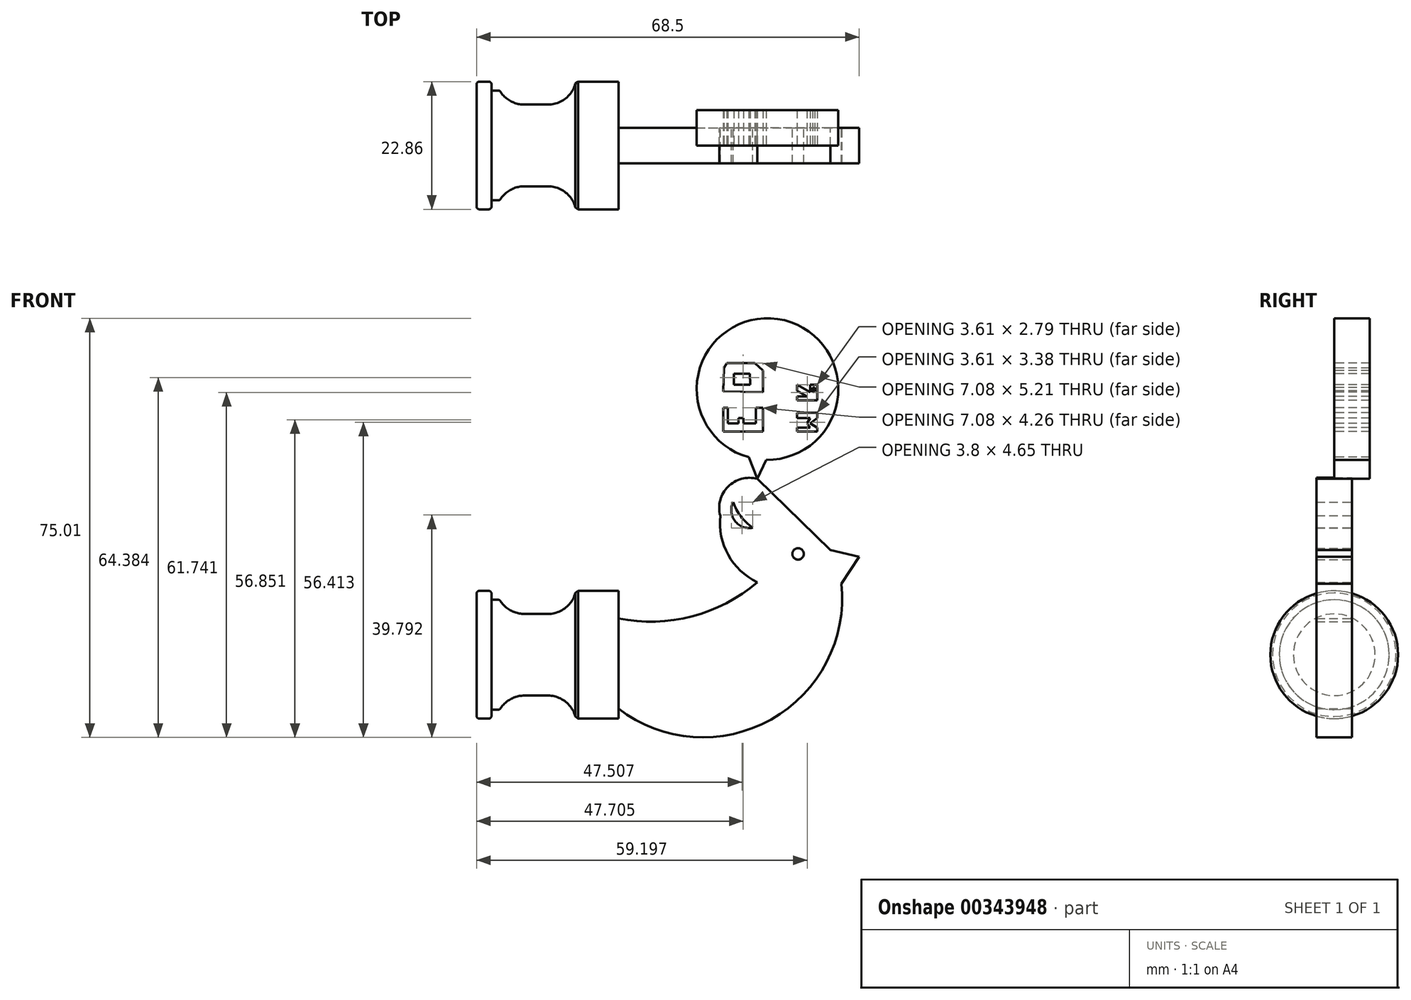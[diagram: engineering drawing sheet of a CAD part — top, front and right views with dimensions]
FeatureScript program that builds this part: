
annotation { "Feature Type Name" : "Feature", "Feature Type Description" : "" }
export const myFeature = defineFeature(function(context is Context, id is Id, definition is map)
    precondition{}
    {
        {
            var Q0;
            Q0=qCreatedBy(makeId("Front.planeOp"),FACE);
            var sketch = newSketch(context, id + "F0", { "sketchPlane" : qUnion([Q0])});
            skLineSegment(sketch, "E0", {"start": v(0, 0) * mm, "end": v(-25.4, 0) * mm});
            skLineSegment(sketch, "E1", {"start": v(-25.4, 0) * mm, "end": v(-25.4, 11.43) * mm});
            skLineSegment(sketch, "E2", {"start": v(-25.4, 11.43) * mm, "end": v(-22.71, 11.43) * mm});
            skLineSegment(sketch, "E3", {"start": v(-22.71, 11.43) * mm, "end": v(-22.71, 9.84) * mm});
            skLineSegment(sketch, "E4", {"start": v(-22.71, 9.84) * mm, "end": v(-21.25, 9.84) * mm});
            skLineSegment(sketch, "E5", {"start": v(-21.25, 9.84) * mm, "end": v(-20.32, 7.31) * mm});
            skLineSegment(sketch, "E6", {"start": v(-20.32, 7.31) * mm, "end": v(-7.62, 7.31) * mm});
            skLineSegment(sketch, "E7", {"start": v(-7.62, 7.31) * mm, "end": v(-7.62, 11.43) * mm});
            skLineSegment(sketch, "E8", {"start": v(-7.62, 11.43) * mm, "end": v(0, 11.43) * mm});
            skLineSegment(sketch, "E9", {"start": v(0, 11.43) * mm, "end": v(0, 0) * mm});
            skSolve(sketch);
        }
        {
            var Q0;
            Q0=makeQuery(id+"F0.imprint","IMPRINT",FACE,{"disambiguationData":[TD([[makeQuery(id+"F0.imprint","IMPRINT",EDGE,{"derivedFrom":sQuery(id+"F0.wireOp",EDGE,"E0")}),-1.0]])]});
            var Q1;
            Q1=sQuery(id+"F0.wireOp",EDGE,"E0");
            revolve(context, id + "F1", {"entities" : qUnion([Q0]), "axis" : qUnion([Q1]), "revolveType" : RevolveType.FULL});
        }
        {
            var Q0;
            Q0=makeQuery(id+"F1.opRevolve","SWEPT_EDGE",EDGE,{"disambiguationData":[OSD([sQuery(id+"F0.wireOp",EDGE,"E5"),sQuery(id+"F0.wireOp",EDGE,"E6")])]});
            fillet(context, id + "F2", {"entities" : qUnion([Q0]), "radius" : 5.08 * mm, "tangentPropagation" : true, "allowEdgeOverflow" : false});
        }
        {
            var Q0;
            Q0=makeQuery(id+"F1.opRevolve","SWEPT_EDGE",EDGE,{"disambiguationData":[OSD([sQuery(id+"F0.wireOp",EDGE,"E6"),sQuery(id+"F0.wireOp",EDGE,"E7")])]});
            fillet(context, id + "F3", {"entities" : qUnion([Q0]), "radius" : 5.08 * mm, "tangentPropagation" : true, "allowEdgeOverflow" : false});
        }
        {
            var Q0;
            Q0=makeQuery(id+"F2.opFillet","BLEND_EDGE",EDGE,{"blendedFrom":[makeQuery(id+"F1.opRevolve","SWEPT_EDGE",EDGE,{"disambiguationData":[OSD([sQuery(id+"F0.wireOp",EDGE,"E5"),sQuery(id+"F0.wireOp",EDGE,"E6")])]}),makeQuery(id+"F1.opRevolve","SWEPT_FACE",FACE,{"disambiguationData":[OSD([sQuery(id+"F0.wireOp",EDGE,"E4")])]})],"blendedInto":[makeQuery(id+"F1.opRevolve","SWEPT_FACE",FACE,{"disambiguationData":[OSD([sQuery(id+"F0.wireOp",EDGE,"E4")])]})]});
            var Q1;
            Q1=makeQuery(id+"F1.opRevolve","SWEPT_EDGE",EDGE,{"disambiguationData":[OSD([sQuery(id+"F0.wireOp",EDGE,"E2"),sQuery(id+"F0.wireOp",EDGE,"E3")])]});
            var Q2;
            Q2=makeQuery(id+"F1.opRevolve","SWEPT_EDGE",EDGE,{"disambiguationData":[OSD([sQuery(id+"F0.wireOp",EDGE,"E1"),sQuery(id+"F0.wireOp",EDGE,"E2")])]});
            fillet(context, id + "F4", {"entities" : qUnion([Q0, Q1, Q2]), "radius" : 0.5 * mm, "tangentPropagation" : true, "allowEdgeOverflow" : false});
        }
        {
            var Q0;
            {var subQ0=sQuery(id+"F0.wireOp",EDGE,"E9");var subQ1=sQuery(id+"F0.wireOp",EDGE,"E8");var subQ2=makeQuery(id+"F1.opRevolve","SWEPT_EDGE",EDGE,{"disambiguationData":[OSD([subQ1,subQ0])]});Q0=makeQuery(id+"F3.opFillet","BLEND_EDGE",EDGE,{"blendedFrom":[makeQuery(id+"F1.opRevolve","SWEPT_EDGE",EDGE,{"disambiguationData":[OSD([sQuery(id+"F0.wireOp",EDGE,"E6"),sQuery(id+"F0.wireOp",EDGE,"E7")])]}),makeQuery(id+"FKdUeLkxdvxAeGn_1.boolean.opBoolean","MERGE",FACE,{"derivedFrom":[makeQuery(id+"F1.opRevolve","SWEPT_FACE",FACE,{"disambiguationData":[OSD([subQ1])]}),makeQuery(id+"FKdUeLkxdvxAeGn_1.opExtrude","SWEPT_FACE",FACE,{"disambiguationData":[OSD([subQ1,subQ0]),TDD([makeQuery(id+"FhPrJ5y7E5olnpu_1.imprint","IMPRINT",EDGE,{"disambiguationData":[TD([[makeQuery(id+"FhPrJ5y7E5olnpu_1.imprint","INTERSECT",VERTEX,{"derivedFrom":[subQ2,sQuery(id+"FhPrJ5y7E5olnpu_1.wireOp",EDGE,"5swccAFu-Qq9y-H5FG-WLZN-0cyFNXjqbd3L")]}),1.0]])],"derivedFrom":subQ2})])]}),makeQuery(id+"FKdUeLkxdvxAeGn_1.opExtrude","SWEPT_FACE",FACE,{"disambiguationData":[OSD([subQ1,subQ0]),TDD([makeQuery(id+"FhPrJ5y7E5olnpu_1.imprint","IMPRINT",EDGE,{"disambiguationData":[TD([[makeQuery(id+"FhPrJ5y7E5olnpu_1.imprint","INTERSECT",VERTEX,{"derivedFrom":[subQ2,sQuery(id+"FhPrJ5y7E5olnpu_1.wireOp",EDGE,"yrlBlJsE-glzK-ckup-w4H4-O8etLDBYbZ2E")]}),1.0]])],"derivedFrom":subQ2})])]}),makeQuery(id+"FKdUeLkxdvxAeGn_1.opExtrude","SWEPT_FACE",FACE,{"disambiguationData":[OSD([subQ1,subQ0]),TDD([makeQuery(id+"FhPrJ5y7E5olnpu_1.imprint","IMPRINT",EDGE,{"disambiguationData":[TD([[makeQuery(id+"FhPrJ5y7E5olnpu_1.imprint","INTERSECT",VERTEX,{"derivedFrom":[subQ2,sQuery(id+"FhPrJ5y7E5olnpu_1.wireOp",EDGE,"59esLNOy-bGTi-q598-Dafd-GjDcgzXxW0rH")]}),-1.0]])],"derivedFrom":subQ2})])]}),makeQuery(id+"FKdUeLkxdvxAeGn_1.opExtrude","SWEPT_FACE",FACE,{"disambiguationData":[OSD([subQ1,subQ0]),TDD([makeQuery(id+"FhPrJ5y7E5olnpu_1.imprint","IMPRINT",EDGE,{"disambiguationData":[TD([[makeQuery(id+"FhPrJ5y7E5olnpu_1.imprint","INTERSECT",VERTEX,{"derivedFrom":[subQ2,sQuery(id+"FhPrJ5y7E5olnpu_1.wireOp",EDGE,"8v8Xe1NO-uW00-CEbA-Of9p-lGgIFj4n3XNv")]}),-1.0]])],"derivedFrom":subQ2})])]})]})],"blendedInto":[makeQuery(id+"FKdUeLkxdvxAeGn_1.boolean.opBoolean","MERGE",FACE,{"derivedFrom":[makeQuery(id+"F1.opRevolve","SWEPT_FACE",FACE,{"disambiguationData":[OSD([subQ1])]}),makeQuery(id+"FKdUeLkxdvxAeGn_1.opExtrude","SWEPT_FACE",FACE,{"disambiguationData":[OSD([subQ1,subQ0]),TDD([makeQuery(id+"FhPrJ5y7E5olnpu_1.imprint","IMPRINT",EDGE,{"disambiguationData":[TD([[makeQuery(id+"FhPrJ5y7E5olnpu_1.imprint","INTERSECT",VERTEX,{"derivedFrom":[subQ2,sQuery(id+"FhPrJ5y7E5olnpu_1.wireOp",EDGE,"5swccAFu-Qq9y-H5FG-WLZN-0cyFNXjqbd3L")]}),1.0]])],"derivedFrom":subQ2})])]}),makeQuery(id+"FKdUeLkxdvxAeGn_1.opExtrude","SWEPT_FACE",FACE,{"disambiguationData":[OSD([subQ1,subQ0]),TDD([makeQuery(id+"FhPrJ5y7E5olnpu_1.imprint","IMPRINT",EDGE,{"disambiguationData":[TD([[makeQuery(id+"FhPrJ5y7E5olnpu_1.imprint","INTERSECT",VERTEX,{"derivedFrom":[subQ2,sQuery(id+"FhPrJ5y7E5olnpu_1.wireOp",EDGE,"yrlBlJsE-glzK-ckup-w4H4-O8etLDBYbZ2E")]}),1.0]])],"derivedFrom":subQ2})])]}),makeQuery(id+"FKdUeLkxdvxAeGn_1.opExtrude","SWEPT_FACE",FACE,{"disambiguationData":[OSD([subQ1,subQ0]),TDD([makeQuery(id+"FhPrJ5y7E5olnpu_1.imprint","IMPRINT",EDGE,{"disambiguationData":[TD([[makeQuery(id+"FhPrJ5y7E5olnpu_1.imprint","INTERSECT",VERTEX,{"derivedFrom":[subQ2,sQuery(id+"FhPrJ5y7E5olnpu_1.wireOp",EDGE,"59esLNOy-bGTi-q598-Dafd-GjDcgzXxW0rH")]}),-1.0]])],"derivedFrom":subQ2})])]}),makeQuery(id+"FKdUeLkxdvxAeGn_1.opExtrude","SWEPT_FACE",FACE,{"disambiguationData":[OSD([subQ1,subQ0]),TDD([makeQuery(id+"FhPrJ5y7E5olnpu_1.imprint","IMPRINT",EDGE,{"disambiguationData":[TD([[makeQuery(id+"FhPrJ5y7E5olnpu_1.imprint","INTERSECT",VERTEX,{"derivedFrom":[subQ2,sQuery(id+"FhPrJ5y7E5olnpu_1.wireOp",EDGE,"8v8Xe1NO-uW00-CEbA-Of9p-lGgIFj4n3XNv")]}),-1.0]])],"derivedFrom":subQ2})])]})]})]});}
            chamfer(context, id + "F5", {"entities" : qUnion([Q0]), "width" : 0.5 * mm, "tangentPropagation" : true});
        }
        {
            var Q0;
            Q0=qCreatedBy(makeId("Front.planeOp"),FACE);
            var sketch = newSketch(context, id + "F6", { "sketchPlane" : qUnion([Q0])});
            skArc(sketch, "E10", {"start": v(0, -9.66) * mm, "mid": v(27.32, -11.6) * mm, "end": v(39.92, 12.73) * mm});
            skLineSegment(sketch, "E11", {"start": v(39.92, 12.73) * mm, "end": v(43.1, 17.57) * mm});
            skLineSegment(sketch, "E12", {"start": v(43.1, 17.57) * mm, "end": v(37.92, 18.75) * mm});
            skLineSegment(sketch, "E13", {"start": v(37.92, 18.75) * mm, "end": v(24.83, 31.48) * mm});
            skArc(sketch, "E14", {"start": v(24.83, 31.48) * mm, "mid": v(19.62, 30.1) * mm, "end": v(18.23, 24.88) * mm});
            skArc(sketch, "E15", {"start": v(18.23, 24.88) * mm, "mid": v(19.65, 17.88) * mm, "end": v(24.83, 12.97) * mm});
            skArc(sketch, "E16", {"start": v(0, 6.5) * mm, "mid": v(13.16, 6.87) * mm, "end": v(24.83, 12.97) * mm});
            skLineSegment(sketch, "E17", {"start": v(0, -9.66) * mm, "end": v(0, 6.5) * mm});
            skSolve(sketch);
        }
        {
            var Q0;
            Q0=makeQuery(id+"F6.imprint","IMPRINT",FACE,{"disambiguationData":[TD([[makeQuery(id+"F6.imprint","IMPRINT",EDGE,{"derivedFrom":sQuery(id+"F6.wireOp",EDGE,"E10")}),1.0]])]});
            extrude(context, id + "F7", {"entities" : qUnion([Q0]), "operationType" : NewBodyOperationType.ADD, "endBound" : BoundingType.SYMMETRIC, "depth" : 6.35 * mm});
        }
        {
            var Q0;
            Q0=makeQuery(id+"F7.opExtrude","CAP_FACE",FACE,{"disambiguationData":[OSD([sQuery(id+"F6.wireOp",EDGE,"E10"),sQuery(id+"F6.wireOp",EDGE,"E11"),sQuery(id+"F6.wireOp",EDGE,"E12"),sQuery(id+"F6.wireOp",EDGE,"E13"),sQuery(id+"F6.wireOp",EDGE,"E14"),sQuery(id+"F6.wireOp",EDGE,"E15"),sQuery(id+"F6.wireOp",EDGE,"E16"),sQuery(id+"F6.wireOp",EDGE,"E17")])],"isStart":true});
            var sketch = newSketch(context, id + "F8", { "sketchPlane" : qUnion([Q0])});
            skCircle(sketch, "E18", {"center": v(-32.15, 18.05) * mm, "radius": 1.16 * mm});
            skSolve(sketch);
        }
        {
            var Q0;
            Q0=sQuery(id+"F8.wireOp",VERTEX,"E18.center");
            var Q1;
            Q1=makeQuery(id+"F1.opRevolve","SWEPT_BODY",BODY,{"disambiguationData":[OSD([sQuery(id+"F0.wireOp",EDGE,"E0"),sQuery(id+"F0.wireOp",EDGE,"E1"),sQuery(id+"F0.wireOp",EDGE,"E2"),sQuery(id+"F0.wireOp",EDGE,"E3"),sQuery(id+"F0.wireOp",EDGE,"E4"),sQuery(id+"F0.wireOp",EDGE,"E5"),sQuery(id+"F0.wireOp",EDGE,"E6"),sQuery(id+"F0.wireOp",EDGE,"E7"),sQuery(id+"F0.wireOp",EDGE,"E8"),sQuery(id+"F0.wireOp",EDGE,"E9")])]});
            hole(context, id + "F9", {"style" : HoleStyle.SIMPLE, "endStyle" : HoleEndStyle.THROUGH, "standardTappedOrClearance" : lookupTablePath({ "standard" : "ANSI", "fit" : "Normal (ASME)", "size" : "#1", "type" : "Clearance" }), "standardBlindInLast" : lookupTablePath({ "fit" : "Free", "standard" : "ANSI", "size" : "#1", "type" : "Clearance" }), "holeDiameter" : 2.06 * mm, "isTappedThrough" : true, "tappedDepth" : 12.7 * mm, "tapClearance" : 3, "locations" : qUnion([Q0]), "scope" : qUnion([Q1])});
        }
        {
            var Q0;
            Q0=makeQuery(id+"F7.opExtrude","CAP_FACE",FACE,{"disambiguationData":[OSD([sQuery(id+"F6.wireOp",EDGE,"E10"),sQuery(id+"F6.wireOp",EDGE,"E11"),sQuery(id+"F6.wireOp",EDGE,"E12"),sQuery(id+"F6.wireOp",EDGE,"E13"),sQuery(id+"F6.wireOp",EDGE,"E14"),sQuery(id+"F6.wireOp",EDGE,"E15"),sQuery(id+"F6.wireOp",EDGE,"E16"),sQuery(id+"F6.wireOp",EDGE,"E17")])],"isStart":true});
            var sketch = newSketch(context, id + "F10", { "sketchPlane" : qUnion([Q0])});
            skArc(sketch, "E19", {"start": v(-24, 22.73) * mm, "mid": v(-21.92, 24.77) * mm, "end": v(-20.53, 27.34) * mm});
            skArc(sketch, "E20", {"start": v(-24, 22.73) * mm, "mid": v(-20.84, 23.96) * mm, "end": v(-20.53, 27.34) * mm});
            skSolve(sketch);
        }
        {
            var Q0;
            Q0=makeQuery(id+"F10.imprint","IMPRINT",FACE,{"disambiguationData":[TD([[makeQuery(id+"F10.imprint","IMPRINT",EDGE,{"derivedFrom":sQuery(id+"F10.wireOp",EDGE,"E19")}),-1.0]])]});
            extrude(context, id + "F11", {"entities" : qUnion([Q0]), "operationType" : NewBodyOperationType.REMOVE, "endBound" : BoundingType.SYMMETRIC, "oppositeDirection" : true, "depth" : 25.4 * mm});
        }
        {
            var Q0;
            Q0=makeQuery(id+"F7.opExtrude","CAP_FACE",FACE,{"disambiguationData":[OSD([sQuery(id+"F6.wireOp",EDGE,"E10"),sQuery(id+"F6.wireOp",EDGE,"E11"),sQuery(id+"F6.wireOp",EDGE,"E12"),sQuery(id+"F6.wireOp",EDGE,"E13"),sQuery(id+"F6.wireOp",EDGE,"E14"),sQuery(id+"F6.wireOp",EDGE,"E15"),sQuery(id+"F6.wireOp",EDGE,"E16"),sQuery(id+"F6.wireOp",EDGE,"E17")])],"isStart":true});
            var sketch = newSketch(context, id + "F12", { "sketchPlane" : qUnion([Q0])});
            skLineSegment(sketch, "E21", {"start": v(-24.83, 31.48) * mm, "end": v(-26.47, 34.9) * mm});
            skLineSegment(sketch, "E22", {"start": v(-24.83, 31.48) * mm, "end": v(-23.3, 35.35) * mm});
            skArc(sketch, "E23", {"start": v(-23.3, 35.35) * mm, "mid": v(-28.5, 60.1) * mm, "end": v(-26.47, 34.9) * mm});
            skSolve(sketch);
        }
        {
            var Q0;
            Q0=makeQuery(id+"F12.imprint","IMPRINT",FACE,{"disambiguationData":[TD([[makeQuery(id+"F12.imprint","IMPRINT",EDGE,{"derivedFrom":sQuery(id+"F12.wireOp",EDGE,"E21")}),-1.0]])]});
            extrude(context, id + "F13", {"entities" : qUnion([Q0]), "operationType" : NewBodyOperationType.ADD, "endBound" : BoundingType.SYMMETRIC, "depth" : 6.35 * mm});
        }
        {
            var Q0;
            Q0=makeQuery(id+"F13.opExtrude","CAP_FACE",FACE,{"disambiguationData":[OSD([sQuery(id+"F12.wireOp",EDGE,"E21"),sQuery(id+"F12.wireOp",EDGE,"E22"),sQuery(id+"F12.wireOp",EDGE,"E23")])],"isStart":false});
            var sketch = newSketch(context, id + "F14", { "sketchPlane" : qUnion([Q0])});
            skLineSegment(sketch, "E24", {"start": v(-32, 39.94) * mm, "end": v(-35.6, 39.94) * mm});
            skLineSegment(sketch, "E25", {"start": v(-35.6, 39.94) * mm, "end": v(-35.6, 40.65) * mm});
            skLineSegment(sketch, "E26", {"start": v(-35.6, 40.65) * mm, "end": v(-34.33, 41.39) * mm});
            skLineSegment(sketch, "E27", {"start": v(-34.33, 41.39) * mm, "end": v(-35.6, 42.38) * mm});
            skLineSegment(sketch, "E28", {"start": v(-35.6, 42.38) * mm, "end": v(-35.6, 43.32) * mm});
            skLineSegment(sketch, "E29", {"start": v(-35.6, 43.32) * mm, "end": v(-32, 43.32) * mm});
            skLineSegment(sketch, "E30", {"start": v(-32, 43.32) * mm, "end": v(-32, 42.38) * mm});
            skLineSegment(sketch, "E31", {"start": v(-32, 42.38) * mm, "end": v(-34.33, 42.38) * mm});
            skLineSegment(sketch, "E32", {"start": v(-34.33, 42.38) * mm, "end": v(-33.76, 41.39) * mm});
            skLineSegment(sketch, "E33", {"start": v(-33.76, 41.39) * mm, "end": v(-34.33, 40.65) * mm});
            skLineSegment(sketch, "E34", {"start": v(-34.33, 40.65) * mm, "end": v(-32, 40.65) * mm});
            skLineSegment(sketch, "E35", {"start": v(-32, 40.65) * mm, "end": v(-32, 39.94) * mm});
            skLineSegment(sketch, "E36", {"start": v(-32, 45.57) * mm, "end": v(-35.6, 45.57) * mm});
            skLineSegment(sketch, "E37", {"start": v(-35.6, 45.57) * mm, "end": v(-35.6, 48.36) * mm});
            skLineSegment(sketch, "E38", {"start": v(-35.6, 48.36) * mm, "end": v(-34.33, 48.36) * mm});
            skLineSegment(sketch, "E39", {"start": v(-34.33, 48.36) * mm, "end": v(-34.33, 47) * mm});
            skLineSegment(sketch, "E40", {"start": v(-34.33, 47) * mm, "end": v(-32, 48.36) * mm});
            skLineSegment(sketch, "E41", {"start": v(-32, 48.36) * mm, "end": v(-32, 47.27) * mm});
            skLineSegment(sketch, "E42", {"start": v(-32, 47.27) * mm, "end": v(-33.76, 46.25) * mm});
            skLineSegment(sketch, "E43", {"start": v(-33.76, 46.25) * mm, "end": v(-32, 46.25) * mm});
            skLineSegment(sketch, "E44", {"start": v(-32, 46.25) * mm, "end": v(-32, 45.57) * mm});
            skLineSegment(sketch, "E45", {"start": v(-35.15, 47.16) * mm, "end": v(-34.77, 47) * mm});
            skLineSegment(sketch, "E46", {"start": v(-34.77, 47) * mm, "end": v(-34.77, 47.81) * mm});
            skLineSegment(sketch, "E47", {"start": v(-35.15, 47.16) * mm, "end": v(-35.15, 47.81) * mm});
            skLineSegment(sketch, "E48", {"start": v(-35.15, 47.81) * mm, "end": v(-34.77, 47.81) * mm});
            skLineSegment(sketch, "E49", {"start": v(-25.84, 39.94) * mm, "end": v(-18.77, 39.94) * mm});
            skLineSegment(sketch, "E50", {"start": v(-18.77, 39.94) * mm, "end": v(-18.77, 44.2) * mm});
            skLineSegment(sketch, "E51", {"start": v(-18.77, 44.2) * mm, "end": v(-19.56, 44.2) * mm});
            skLineSegment(sketch, "E52", {"start": v(-19.56, 44.2) * mm, "end": v(-19.56, 41.39) * mm});
            skLineSegment(sketch, "E53", {"start": v(-19.56, 41.39) * mm, "end": v(-21.5, 41.39) * mm});
            skLineSegment(sketch, "E54", {"start": v(-21.5, 41.39) * mm, "end": v(-21.5, 42.38) * mm});
            skLineSegment(sketch, "E55", {"start": v(-21.5, 42.38) * mm, "end": v(-22.37, 42.38) * mm});
            skLineSegment(sketch, "E56", {"start": v(-22.37, 42.38) * mm, "end": v(-22.37, 41.39) * mm});
            skLineSegment(sketch, "E57", {"start": v(-22.37, 41.39) * mm, "end": v(-24.59, 41.39) * mm});
            skLineSegment(sketch, "E58", {"start": v(-24.59, 41.39) * mm, "end": v(-24.59, 44.2) * mm});
            skLineSegment(sketch, "E59", {"start": v(-24.59, 44.2) * mm, "end": v(-25.84, 44.2) * mm});
            skLineSegment(sketch, "E60", {"start": v(-25.84, 44.2) * mm, "end": v(-25.84, 39.94) * mm});
            skLineSegment(sketch, "E61", {"start": v(-25.84, 47) * mm, "end": v(-18.77, 47.16) * mm});
            skLineSegment(sketch, "E62", {"start": v(-18.77, 47.16) * mm, "end": v(-18.86, 51.29) * mm});
            skLineSegment(sketch, "E63", {"start": v(-18.86, 51.29) * mm, "end": v(-19.39, 52.2) * mm});
            skLineSegment(sketch, "E64", {"start": v(-19.39, 52.2) * mm, "end": v(-24.38, 52.2) * mm});
            skLineSegment(sketch, "E65", {"start": v(-24.38, 52.2) * mm, "end": v(-25.84, 50.89) * mm});
            skLineSegment(sketch, "E66", {"start": v(-25.84, 50.89) * mm, "end": v(-25.84, 47) * mm});
            skLineSegment(sketch, "E67", {"start": v(-23.59, 48.36) * mm, "end": v(-20.63, 48.36) * mm});
            skLineSegment(sketch, "E68", {"start": v(-20.63, 48.36) * mm, "end": v(-20.63, 50.33) * mm});
            skLineSegment(sketch, "E69", {"start": v(-20.63, 50.33) * mm, "end": v(-23.49, 50.33) * mm});
            skLineSegment(sketch, "E70", {"start": v(-23.49, 50.33) * mm, "end": v(-23.59, 48.36) * mm});
            skSolve(sketch);
        }
        {
            var Q0;
            Q0=makeQuery(id+"F14.imprint","IMPRINT",FACE,{"disambiguationData":[TD([[makeQuery(id+"F14.imprint","IMPRINT",EDGE,{"derivedFrom":sQuery(id+"F14.wireOp",EDGE,"E24")}),-1.0]])]});
            var Q1;
            Q1=makeQuery(id+"F14.imprint","IMPRINT",FACE,{"disambiguationData":[TD([[makeQuery(id+"F14.imprint","IMPRINT",EDGE,{"derivedFrom":sQuery(id+"F14.wireOp",EDGE,"E36")}),-1.0]])]});
            var Q2;
            Q2=makeQuery(id+"F14.imprint","IMPRINT",FACE,{"disambiguationData":[TD([[makeQuery(id+"F14.imprint","IMPRINT",EDGE,{"derivedFrom":sQuery(id+"F14.wireOp",EDGE,"E49")}),1.0]])]});
            var Q3;
            Q3=makeQuery(id+"F14.imprint","IMPRINT",FACE,{"disambiguationData":[TD([[makeQuery(id+"F14.imprint","IMPRINT",EDGE,{"derivedFrom":sQuery(id+"F14.wireOp",EDGE,"E61")}),1.0]])]});
            extrude(context, id + "F15", {"entities" : qUnion([Q0, Q1, Q2, Q3]), "operationType" : NewBodyOperationType.REMOVE, "endBound" : BoundingType.SYMMETRIC, "depth" : 25.4 * mm});
        }
    });
